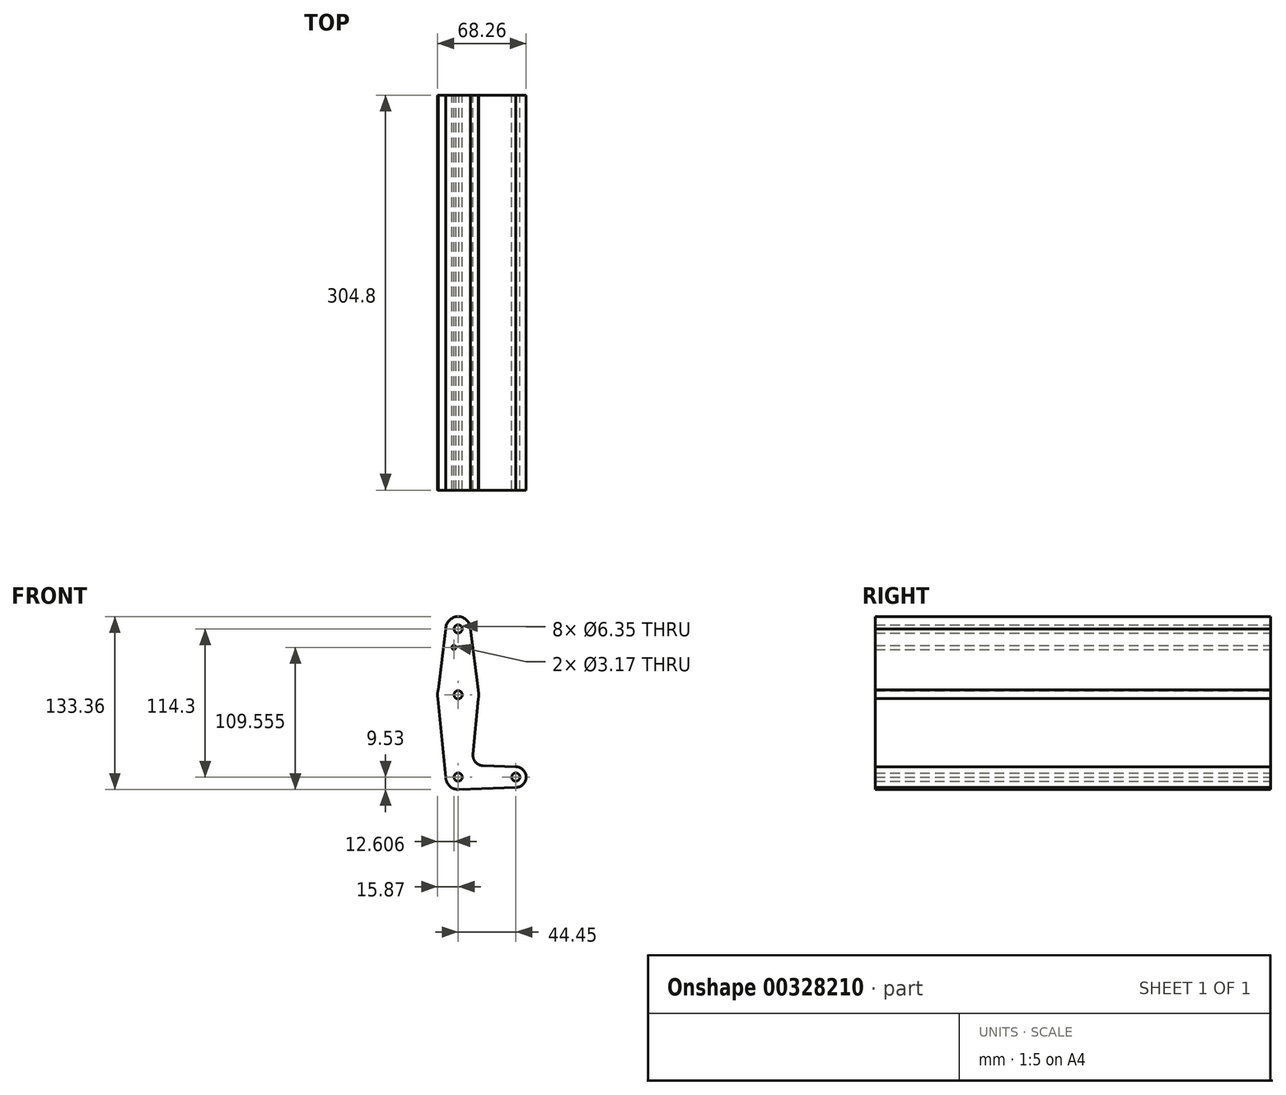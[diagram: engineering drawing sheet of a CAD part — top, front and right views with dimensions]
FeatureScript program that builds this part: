
annotation { "Feature Type Name" : "Feature", "Feature Type Description" : "" }
export const myFeature = defineFeature(function(context is Context, id is Id, definition is map)
    precondition{}
    {
        {
            var Q0;
            Q0=qCreatedBy(makeId("Front.planeOp"),FACE);
            var sketch = newSketch(context, id + "F0", { "sketchPlane" : qUnion([Q0])});
            skCircle(sketch, "E0", {"center": v(0, 114.3) * mm, "radius": 9.53 * mm});
            skCircle(sketch, "E1", {"center": v(0, 0) * mm, "radius": 9.53 * mm});
            skCircle(sketch, "E2", {"center": v(44.45, 0) * mm, "radius": 7.94 * mm});
            skCircle(sketch, "E3", {"center": v(0, 63.5) * mm, "radius": 15.88 * mm});
            skLineSegment(sketch, "E4", {"start": v(-9.53, 114.3) * mm, "end": v(-15.88, 63.5) * mm});
            skLineSegment(sketch, "E5", {"start": v(9.52, 114.3) * mm, "end": v(15.88, 63.5) * mm});
            skLineSegment(sketch, "E6", {"start": v(-15.88, 63.5) * mm, "end": v(-9.52, 0) * mm});
            skLineSegment(sketch, "E7", {"start": v(15.88, 63.5) * mm, "end": v(11.42, 17.56) * mm});
            skLineSegment(sketch, "E8", {"start": v(19.05, 8.84) * mm, "end": v(44.45, 7.94) * mm});
            skLineSegment(sketch, "E9", {"start": v(0, -9.52) * mm, "end": v(44.45, -7.94) * mm});
            skCircle(sketch, "E10", {"center": v(0, 114.3) * mm, "radius": 3.18 * mm});
            skCircle(sketch, "E11", {"center": v(0, 63.5) * mm, "radius": 3.18 * mm});
            skCircle(sketch, "E12", {"center": v(0, 0) * mm, "radius": 3.18 * mm});
            skCircle(sketch, "E13", {"center": v(44.45, 0) * mm, "radius": 3.18 * mm});
            skArc(sketch, "E14.filletArc", {"start": v(11.42, 17.56) * mm, "mid": v(13.35, 11.55) * mm, "end": v(19.05, 8.84) * mm});
            skLineSegment(sketch, "E15", {"start": v(0, 114.3) * mm, "end": v(0, 0) * mm, "construction": true});
            skLineSegment(sketch, "E16", {"start": v(0, 0) * mm, "end": v(44.45, 0) * mm, "construction": true});
            skCircle(sketch, "E17", {"center": v(-3.26, 100.03) * mm, "radius": 1.59 * mm});
            skSolve(sketch);
        }
        {
            var Q0;
            Q0 = qSketchRegion(id + "F0", true);
            extrude(context, id + "F1", {"entities" : qUnion([Q0]), "depth" : 304.8 * mm});
        }
        {
            var Q0;
            Q0 = qSketchRegion(id + "F0", true);
            extrude(context, id + "F2", {"entities" : qUnion([Q0]), "depth" : 304.8 * mm});
        }
    });
